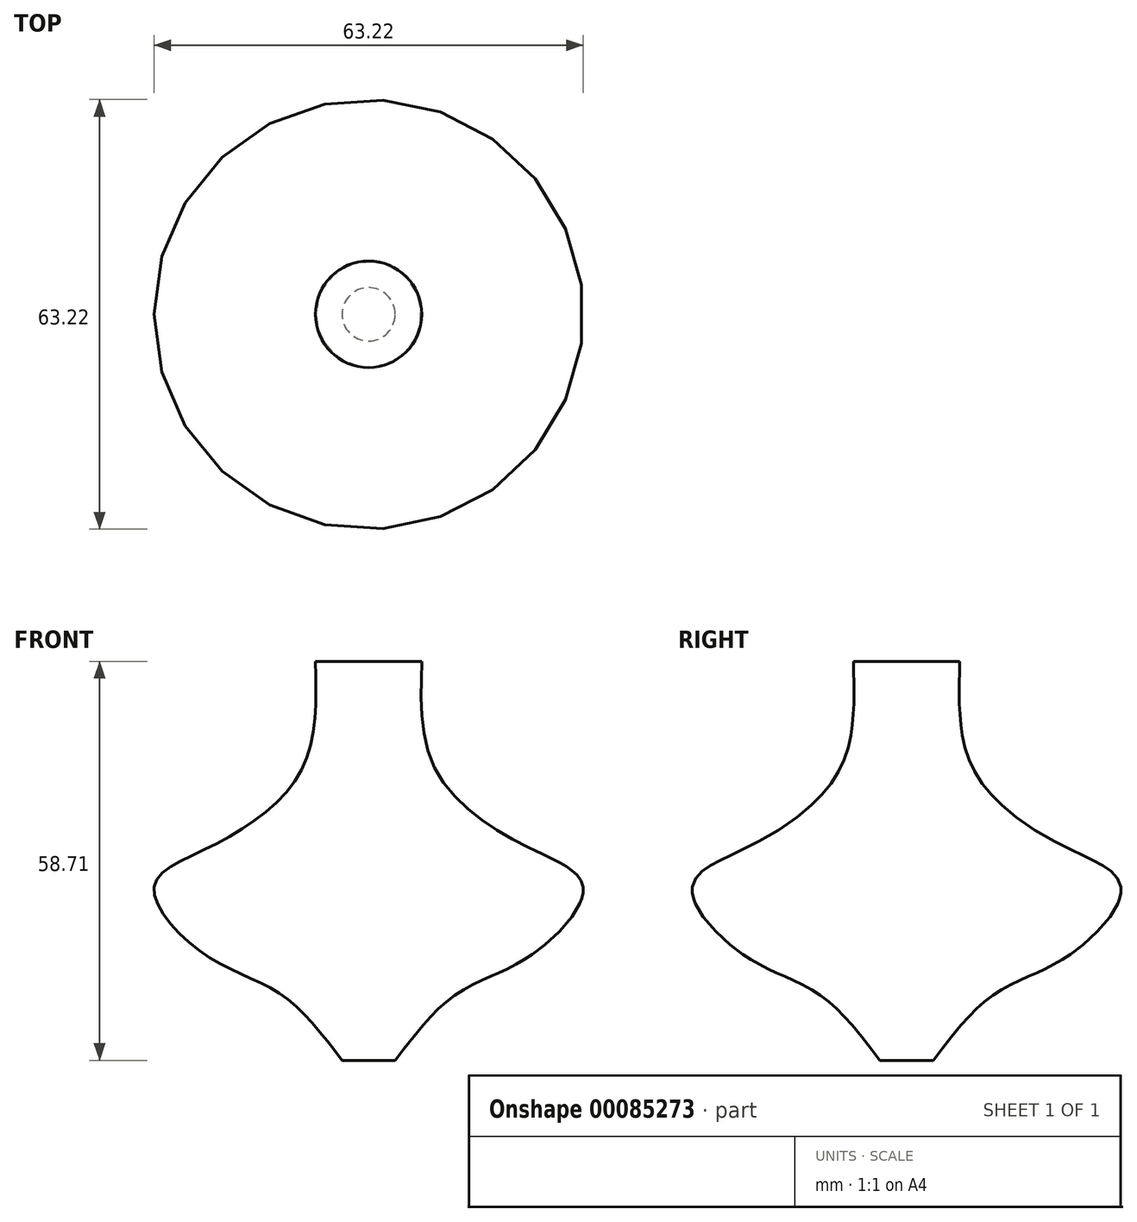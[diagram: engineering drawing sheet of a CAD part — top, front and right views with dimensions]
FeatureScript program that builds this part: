
annotation { "Feature Type Name" : "Feature", "Feature Type Description" : "" }
export const myFeature = defineFeature(function(context is Context, id is Id, definition is map)
    precondition{}
    {
        {
            var Q0;
            Q0=qCreatedBy(makeId("Front.planeOp"),FACE);
            var sketch = newSketch(context, id + "F0", { "sketchPlane" : qUnion([Q0])});
            skLineSegment(sketch, "E0", {"start": v(0, 0) * mm, "end": v(-31.59, 0) * mm});
            skLineSegment(sketch, "E1", {"start": v(0, 0) * mm, "end": v(0, -25.48) * mm});
            skLineSegment(sketch, "E2", {"start": v(0, 0) * mm, "end": v(0, 33.23) * mm});
            skLineSegment(sketch, "E3", {"start": v(0, -25.48) * mm, "end": v(-3.92, -25.48) * mm});
            skLineSegment(sketch, "E4", {"start": v(0, 33.23) * mm, "end": v(-7.83, 33.23) * mm});
            skFitSpline(sketch, "E5", {"points": [v(-7.83, 33.23) * mm, v(-10.05, 16.94) * mm, v(-23.5, 5.87) * mm, v(-31.59, 0) * mm, v(-24, -9.96) * mm, v(-12.94, -15.75) * mm, v(-3.92, -25.48) * mm], "startDerivative": vector(2.91, -94.82) * mm, "endDerivative": vector(51.21, -67.6) * mm});
            skSolve(sketch);
        }
        {
            var Q0;
            {var subQ0=sQuery(id+"F0.wireOp",EDGE,"E0");Q0=makeQuery(id+"F0.imprint","IMPRINT",FACE,{"disambiguationData":[TD([[makeQuery(id+"F0.imprint","IMPRINT",EDGE,{"derivedFrom":subQ0}),-1.0]])]});}
            var Q1;
            {var subQ0=sQuery(id+"F0.wireOp",EDGE,"E0");Q1=makeQuery(id+"F0.imprint","IMPRINT",FACE,{"disambiguationData":[TD([[makeQuery(id+"F0.imprint","IMPRINT",EDGE,{"derivedFrom":subQ0}),1.0]])]});}
            var Q2;
            Q2=sQuery(id+"F0.wireOp",EDGE,"E2");
            revolve(context, id + "F1", {"entities" : qUnion([Q0, Q1]), "axis" : qUnion([Q2]), "revolveType" : RevolveType.FULL});
        }
    });
